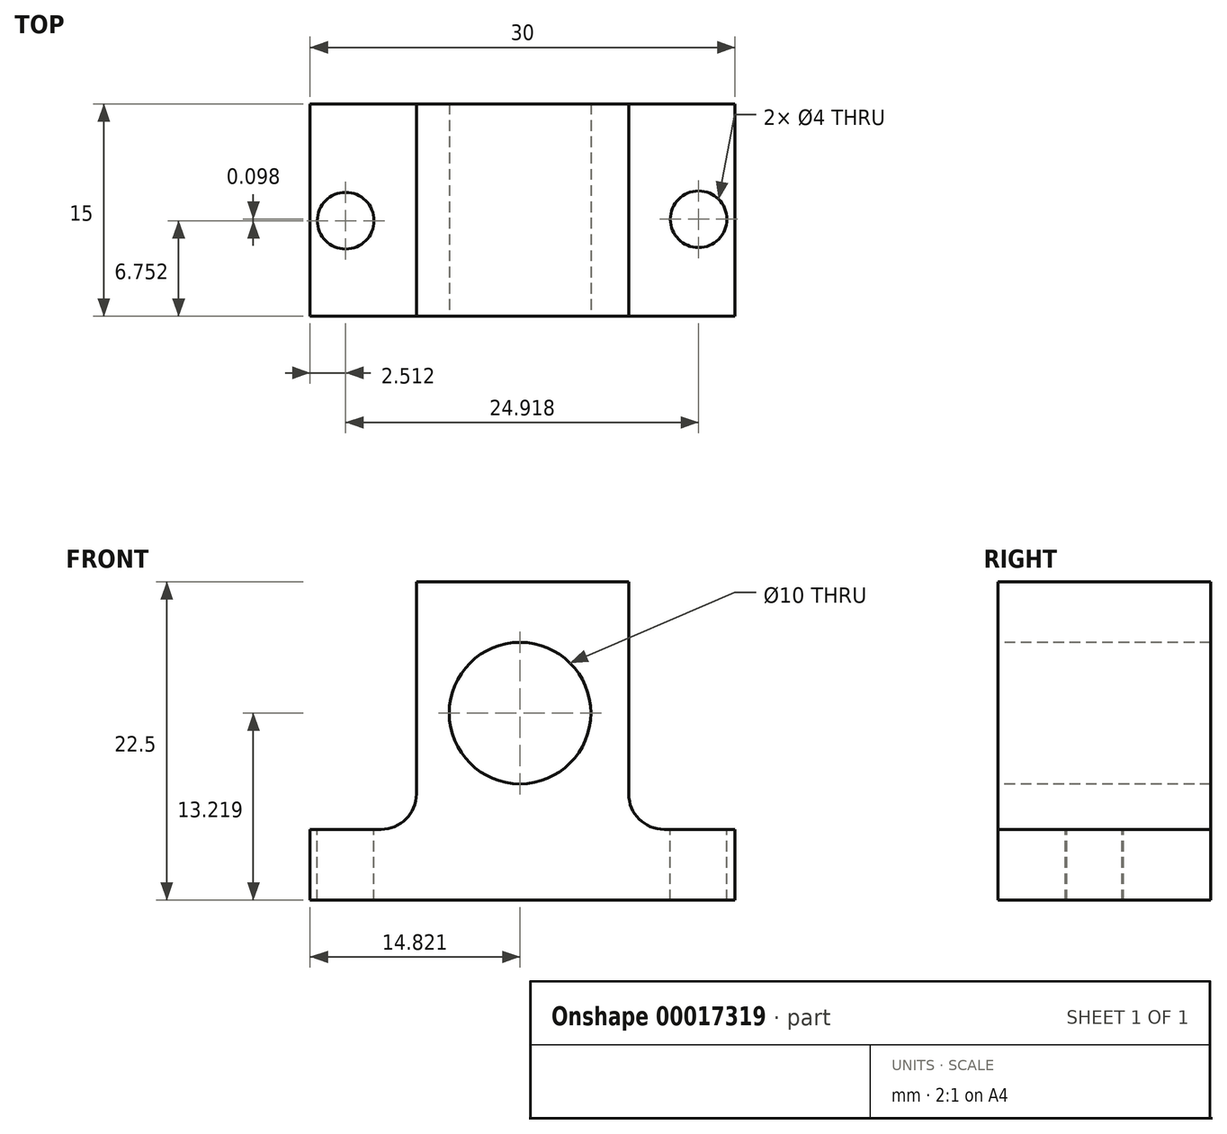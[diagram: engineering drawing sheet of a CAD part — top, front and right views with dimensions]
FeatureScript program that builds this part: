
annotation { "Feature Type Name" : "Feature", "Feature Type Description" : "" }
export const myFeature = defineFeature(function(context is Context, id is Id, definition is map)
    precondition{}
    {
        {
            var Q0;
            Q0=qCreatedBy(makeId("Front.planeOp"),FACE);
            var sketch = newSketch(context, id + "F0", { "sketchPlane" : qUnion([Q0])});
            skLineSegment(sketch, "E0", {"start": v(-23.04, 17.5) * mm, "end": v(-8.04, 17.5) * mm});
            skLineSegment(sketch, "E1", {"start": v(-23.04, 17.5) * mm, "end": v(-23.04, 2.5) * mm});
            skLineSegment(sketch, "E2", {"start": v(-8.04, 17.5) * mm, "end": v(-8.04, 2.5) * mm});
            skLineSegment(sketch, "E3", {"start": v(-5.54, 0) * mm, "end": v(-0.54, 0) * mm});
            skLineSegment(sketch, "E4", {"start": v(-25.54, 0) * mm, "end": v(-30.54, 0) * mm});
            skLineSegment(sketch, "E5", {"start": v(-30.54, 0) * mm, "end": v(-30.54, -5) * mm});
            skLineSegment(sketch, "E6", {"start": v(-0.54, 0) * mm, "end": v(-0.54, -5) * mm});
            skLineSegment(sketch, "E7", {"start": v(-0.54, -5) * mm, "end": v(-30.54, -5) * mm});
            skPoint(sketch, "E8.visualSharp", {"position": v(-23.04, 0) * mm});
            skArc(sketch, "E8.filletArc", {"start": v(-25.54, 0) * mm, "mid": v(-23.77, 0.73) * mm, "end": v(-23.04, 2.5) * mm});
            skPoint(sketch, "E9.visualSharp", {"position": v(-8.04, 0) * mm});
            skArc(sketch, "E9.filletArc", {"start": v(-8.04, 2.5) * mm, "mid": v(-7.3, 0.73) * mm, "end": v(-5.54, 0) * mm});
            skSolve(sketch);
        }
        {
            var Q0;
            Q0 = qSketchRegion(id + "F0", true);
            extrude(context, id + "F1", {"entities" : qUnion([Q0]), "depth" : 15 * mm});
        }
        {
            var Q0;
            Q0=makeQuery(id+"F1.opExtrude","CAP_FACE",FACE,{"disambiguationData":[OSD([sQuery(id+"F0.wireOp",EDGE,"E0"),sQuery(id+"F0.wireOp",EDGE,"E1"),sQuery(id+"F0.wireOp",EDGE,"E2"),sQuery(id+"F0.wireOp",EDGE,"E3"),sQuery(id+"F0.wireOp",EDGE,"E4"),sQuery(id+"F0.wireOp",EDGE,"E5"),sQuery(id+"F0.wireOp",EDGE,"E6"),sQuery(id+"F0.wireOp",EDGE,"E7"),sQuery(id+"F0.wireOp",EDGE,"E8.filletArc"),sQuery(id+"F0.wireOp",EDGE,"E9.filletArc")])],"isStart":false});
            var sketch = newSketch(context, id + "F2", { "sketchPlane" : qUnion([Q0])});
            skCircle(sketch, "E10", {"center": v(-15.72, 8.22) * mm, "radius": 5 * mm});
            skSolve(sketch);
        }
        {
            var Q0;
            Q0=makeQuery(id+"F1.opExtrude","SWEPT_FACE",FACE,{"disambiguationData":[OSD([sQuery(id+"F0.wireOp",EDGE,"E3")])]});
            var sketch = newSketch(context, id + "F3", { "sketchPlane" : qUnion([Q0])});
            skCircle(sketch, "E11", {"center": v(-3.1, -8.15) * mm, "radius": 2 * mm});
            skSolve(sketch);
        }
        {
            var Q0;
            Q0=makeQuery(id+"F1.opExtrude","SWEPT_FACE",FACE,{"disambiguationData":[OSD([sQuery(id+"F0.wireOp",EDGE,"E4")])]});
            var sketch = newSketch(context, id + "F4", { "sketchPlane" : qUnion([Q0])});
            skCircle(sketch, "E12", {"center": v(-28.03, -8.25) * mm, "radius": 2 * mm});
            skSolve(sketch);
        }
        {
            var Q0;
            Q0=makeQuery(id+"F2.imprint","IMPRINT",FACE,{"disambiguationData":[TD([[makeQuery(id+"F2.imprint","IMPRINT",EDGE,{"derivedFrom":sQuery(id+"F2.wireOp",EDGE,"E10")}),1.0]])]});
            extrude(context, id + "F5", {"entities" : qUnion([Q0]), "operationType" : NewBodyOperationType.REMOVE, "endBound" : BoundingType.THROUGH_ALL, "oppositeDirection" : true, "depth" : 15 * mm});
        }
        {
            var Q0;
            Q0=makeQuery(id+"F3.imprint","IMPRINT",FACE,{"disambiguationData":[TD([[makeQuery(id+"F3.imprint","IMPRINT",EDGE,{"derivedFrom":sQuery(id+"F3.wireOp",EDGE,"E11")}),1.0]])]});
            extrude(context, id + "F6", {"entities" : qUnion([Q0]), "operationType" : NewBodyOperationType.REMOVE, "endBound" : BoundingType.THROUGH_ALL, "oppositeDirection" : true, "depth" : 5 * mm});
        }
        {
            var Q0;
            Q0=makeQuery(id+"F4.imprint","IMPRINT",FACE,{"disambiguationData":[TD([[makeQuery(id+"F4.imprint","IMPRINT",EDGE,{"derivedFrom":sQuery(id+"F4.wireOp",EDGE,"E12")}),1.0]])]});
            extrude(context, id + "F7", {"entities" : qUnion([Q0]), "operationType" : NewBodyOperationType.REMOVE, "endBound" : BoundingType.THROUGH_ALL, "oppositeDirection" : true, "depth" : 5 * mm});
        }
    });
